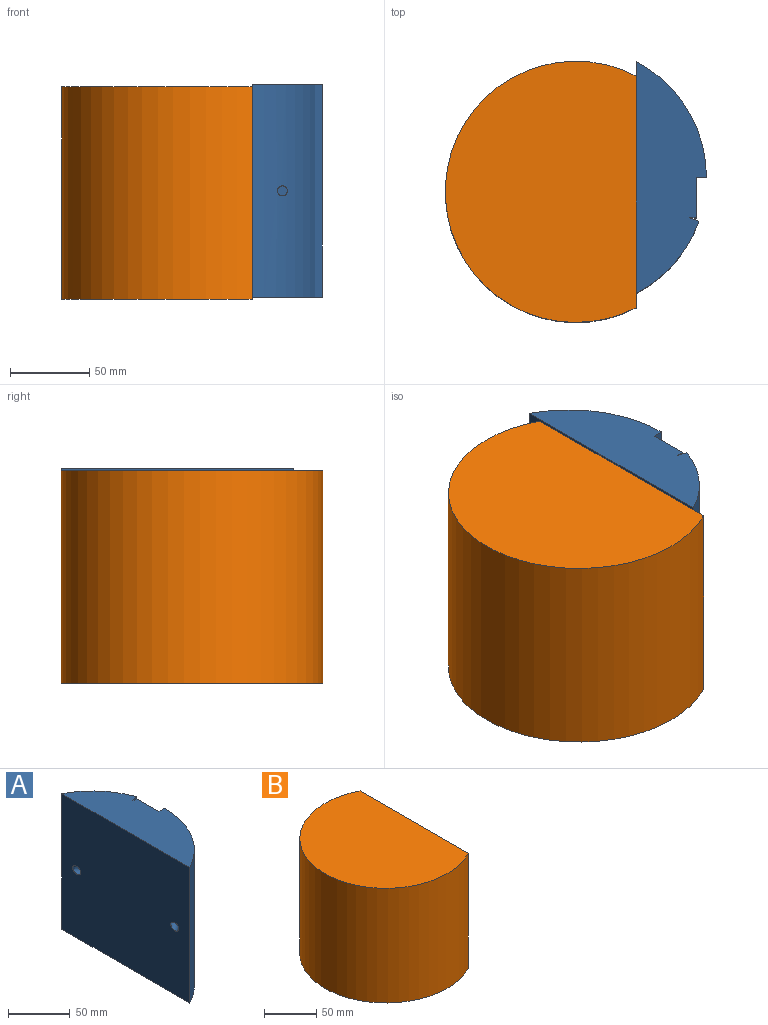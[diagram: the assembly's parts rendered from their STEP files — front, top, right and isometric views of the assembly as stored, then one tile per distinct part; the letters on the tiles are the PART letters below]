
ASSEMBLY  parts=2 mates=2
PART A: 14 faces, bbox 48.6x146.3x134.2 mm
  f0: cylinder r=82.38mm len=134.09mm, axis (0,0,1), area 8246.7mm2, adj f3,f4,f6,f8,f13
  f1: cylinder r=82.38mm len=134.09mm, axis (0,0,1), area 12053.3mm2, adj f3,f4,f7,f13
  f2: plane 134.09x4.37mm, normal (0,1,0), area 585.7mm2, adj f3,f4,f5,f6
  f3: plane 146.17x44.37mm, normal (0,0,1), area 4492.2mm2, adj f0,f1,f2,f5,f6,f7,f13
  f4: plane 146.17x44.37mm, normal (0,0,-1), area 4492.2mm2, adj f0,f1,f2,f5,f6,f7,f13
  f5: plane 134.09x25.4mm, normal (1,0,0), area 3405.8mm2, adj f2,f3,f4,f7
  f6: plane 134.09x5.99mm, normal (0.33,-0.94,0), area 851.5mm2, adj f0,f2,f3,f4
  f7: plane 134.09x6.35mm, normal (0,1,0), area 851.5mm2, adj f1,f3,f4,f5
  f8: cylinder r=3.17mm len=23.64mm, axis (0,-1,0), area 351mm2, adj f0,f9
  f9: torus R=67.78mm, axis (0,0,1), area 2693mm2, adj f8,f10,f11,f12,f13
  f10: plane 11.6x7.78mm, normal (0,1,0), area 64mm2, adj f9,f11,f12
  f11: cylinder r=3.82mm len=25.4mm, axis (0,1,0), area 263.5mm2, adj f9,f10
  f12: cylinder r=3.17mm len=8.97mm, axis (0,-1,0), area 105.3mm2, adj f9,f10
  f13: plane 146.17x134.09mm, normal (-1,0,0), area 19488.8mm2, adj f0,f1,f3,f4,f9
PART B: 5 faces, bbox 128.4x164.8x134.1 mm
  f0: torus R=67.78mm, axis (0,0,1), area 7052.7mm2, adj f1
  f1: plane 146.17x134.09mm, normal (1,0,0), area 19488.8mm2, adj f0,f2,f3,f4
  f2: plane 164.76x120.4mm, normal (0,0,-1), area 16694.3mm2, adj f1,f4
  f3: plane 164.76x120.4mm, normal (0,0,1), area 16694.3mm2, adj f1,f4
  f4: cylinder r=82.38mm len=164.76mm, axis (0,0,1), area 45299.6mm2, adj f1,f2,f3
PLACE A rot(axis=(1,0,0),180deg) t=(144.68,58.16,-48.14)mm
PLACE B t=(144.68,99.88,-49.59)mm
MATE fastened B.f1 <-> A.f13  axis (1,0,0) through (144.68,22.96,-48.83)mm
MATE parallel B.f2 <-> A.f0  axis (0,0,-1) through (91.07,74.48,-116.63)mm
